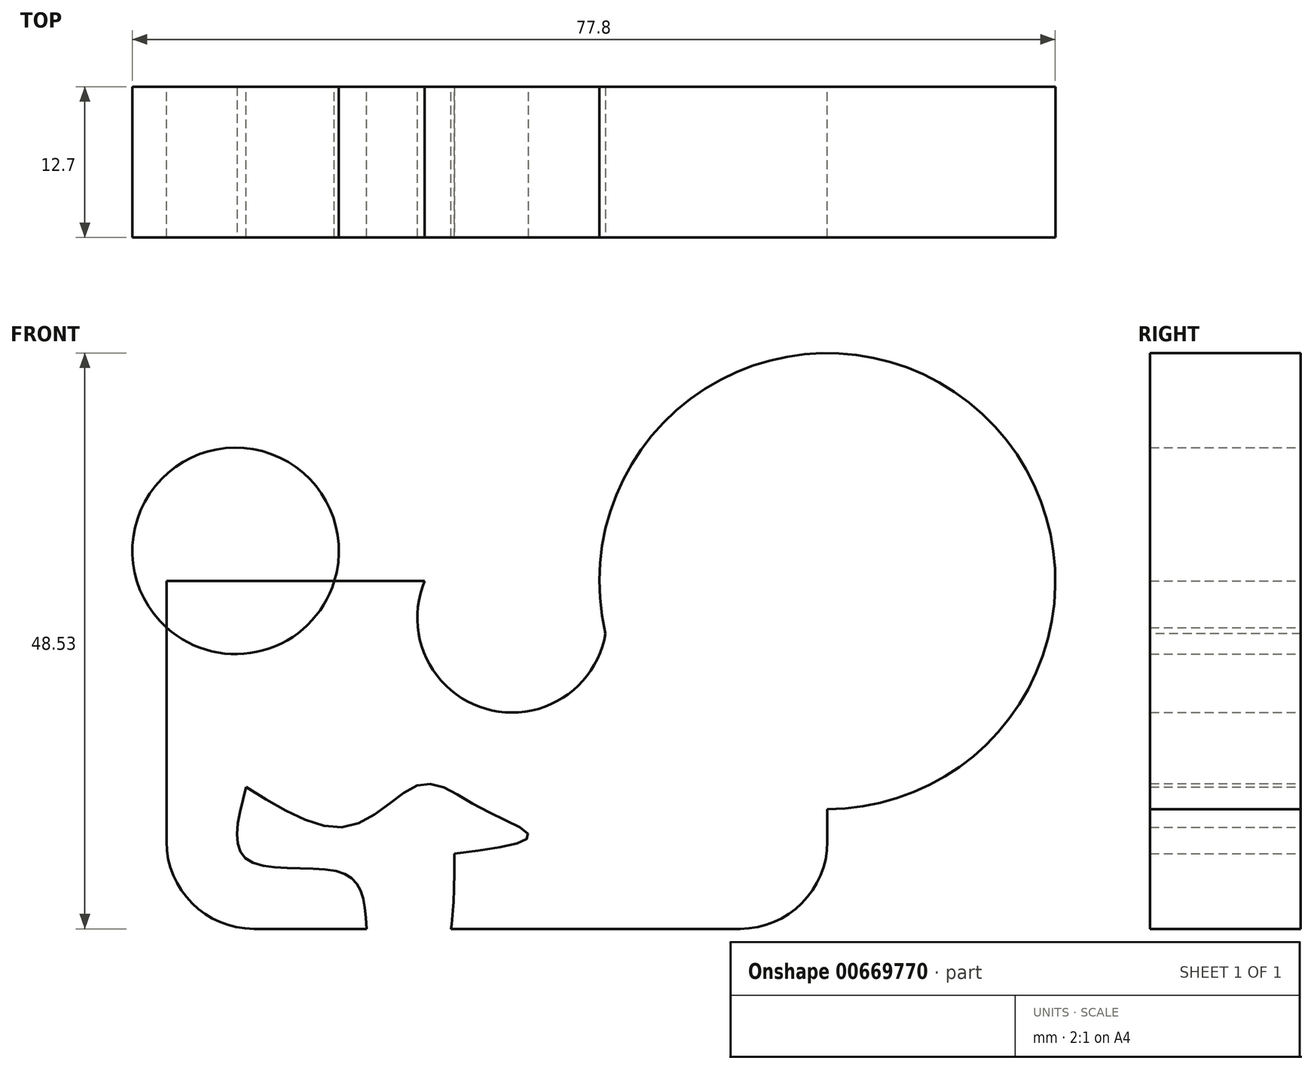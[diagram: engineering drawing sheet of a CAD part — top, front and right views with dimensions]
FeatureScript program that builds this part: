
annotation { "Feature Type Name" : "Feature", "Feature Type Description" : "" }
export const myFeature = defineFeature(function(context is Context, id is Id, definition is map)
    precondition{}
    {
        {
            var Q0;
            Q0=qCreatedBy(makeId("Front.planeOp"),FACE);
            var sketch = newSketch(context, id + "F0", { "sketchPlane" : qUnion([Q0])});
            skLineSegment(sketch, "E0.bottom", {"start": v(0, 0) * mm, "end": v(55.7, 0) * mm});
            skLineSegment(sketch, "E0.top", {"start": v(0, -29.3) * mm, "end": v(55.7, -29.3) * mm});
            skLineSegment(sketch, "E0.left", {"start": v(0, 0) * mm, "end": v(0, -29.3) * mm});
            skLineSegment(sketch, "E0.right", {"start": v(55.7, 0) * mm, "end": v(55.7, -29.3) * mm});
            skCircle(sketch, "E1", {"center": v(29.13, -3.1) * mm, "radius": 7.99 * mm});
            skCircle(sketch, "E2", {"center": v(5.83, 2.55) * mm, "radius": 8.7 * mm});
            skFitSpline(sketch, "E3", {"points": [v(6.72, -17.36) * mm, v(15.6, -20.6) * mm, v(21.44, -17.14) * mm, v(26.42, -19.1) * mm, v(30.53, -21.47) * mm, v(24.26, -22.99) * mm], "startDerivative": vector(38.78, -24.36) * mm, "endDerivative": vector(-47, -6.18) * mm});
            skFitSpline(sketch, "E4", {"points": [v(6.72, -17.36) * mm, v(6.72, -23.42) * mm, v(14.51, -24.5) * mm, v(16.68, -27.32) * mm, v(17.76, -34.03) * mm, v(20.58, -35.98) * mm, v(21.66, -35.54) * mm, v(23.6, -31.43) * mm, v(24.26, -24.72) * mm, v(24.26, -22.99) * mm], "startDerivative": vector(-15.32, -57.21) * mm, "endDerivative": vector(-0.16, 20) * mm});
            skSolve(sketch);
        }
        {
            var Q0;
            {var subQ4=sQuery(id+"F0.wireOp",EDGE,"E0.right");Q0=makeQuery(id+"F0.imprint","IMPRINT",FACE,{"disambiguationData":[TD([[makeQuery(id+"F0.imprint","IMPRINT",EDGE,{"derivedFrom":subQ4}),-1.0]])]});}
            extrude(context, id + "F1", {"entities" : qUnion([Q0]), "depth" : 12.7 * mm, "offsetDistance" : 25.4 * mm});
        }
        {
            var Q0;
            {var subQ0=sQuery(id+"F0.wireOp",EDGE,"E0.left");var subQ1=sQuery(id+"F0.wireOp",EDGE,"E0.bottom");var subQ2=makeQuery(id+"F0.imprint","INTERSECT",VERTEX,{"derivedFrom":[subQ1,subQ0]});Q0=makeQuery(id+"F0.imprint","IMPRINT",FACE,{"disambiguationData":[TD([[makeQuery(id+"F0.imprint","IMPRINT",EDGE,{"disambiguationData":[TD([[subQ2,-1.0]])],"derivedFrom":subQ1}),1.0]])]});}
            extrude(context, id + "F2", {"entities" : qUnion([Q0]), "depth" : 12.7 * mm, "offsetDistance" : 25.4 * mm});
        }
        {
            var Q0;
            {var subQ0=sQuery(id+"F0.wireOp",EDGE,"E0.bottom");Q0=makeQuery(id+"F1.opExtrude","SWEPT_FACE",FACE,{"disambiguationData":[OSD([subQ0]),TDD([makeQuery(id+"F0.imprint","IMPRINT",EDGE,{"disambiguationData":[TD([[makeQuery(id+"F0.imprint","INTERSECT",VERTEX,{"derivedFrom":[subQ0,sQuery(id+"F0.wireOp",EDGE,"E0.right")]}),1.0]])],"derivedFrom":subQ0})])]});}
            var Q1;
            Q1=makeQuery(id+"F1.opExtrude","SWEPT_EDGE",EDGE,{"disambiguationData":[OSD([sQuery(id+"F0.wireOp",EDGE,"E0.bottom"),sQuery(id+"F0.wireOp",EDGE,"E0.right")])]});
            revolve(context, id + "F3", {"operationType" : NewBodyOperationType.ADD, "entities" : qUnion([Q0]), "axis" : qUnion([Q1]), "revolveType" : RevolveType.FULL});
        }
        {
            var Q0;
            Q0=makeQuery(id+"F1.opExtrude","SWEPT_EDGE",EDGE,{"disambiguationData":[OSD([sQuery(id+"F0.wireOp",EDGE,"E0.top"),sQuery(id+"F0.wireOp",EDGE,"E0.right")])]});
            var Q1;
            Q1=makeQuery(id+"F1.opExtrude","SWEPT_EDGE",EDGE,{"disambiguationData":[OSD([sQuery(id+"F0.wireOp",EDGE,"E0.top"),sQuery(id+"F0.wireOp",EDGE,"E0.left")])]});
            fillet(context, id + "F4", {"entities" : qUnion([Q0, Q1]), "radius" : 7.36 * mm, "tangentPropagation" : true, "allowEdgeOverflow" : false});
        }
    });
